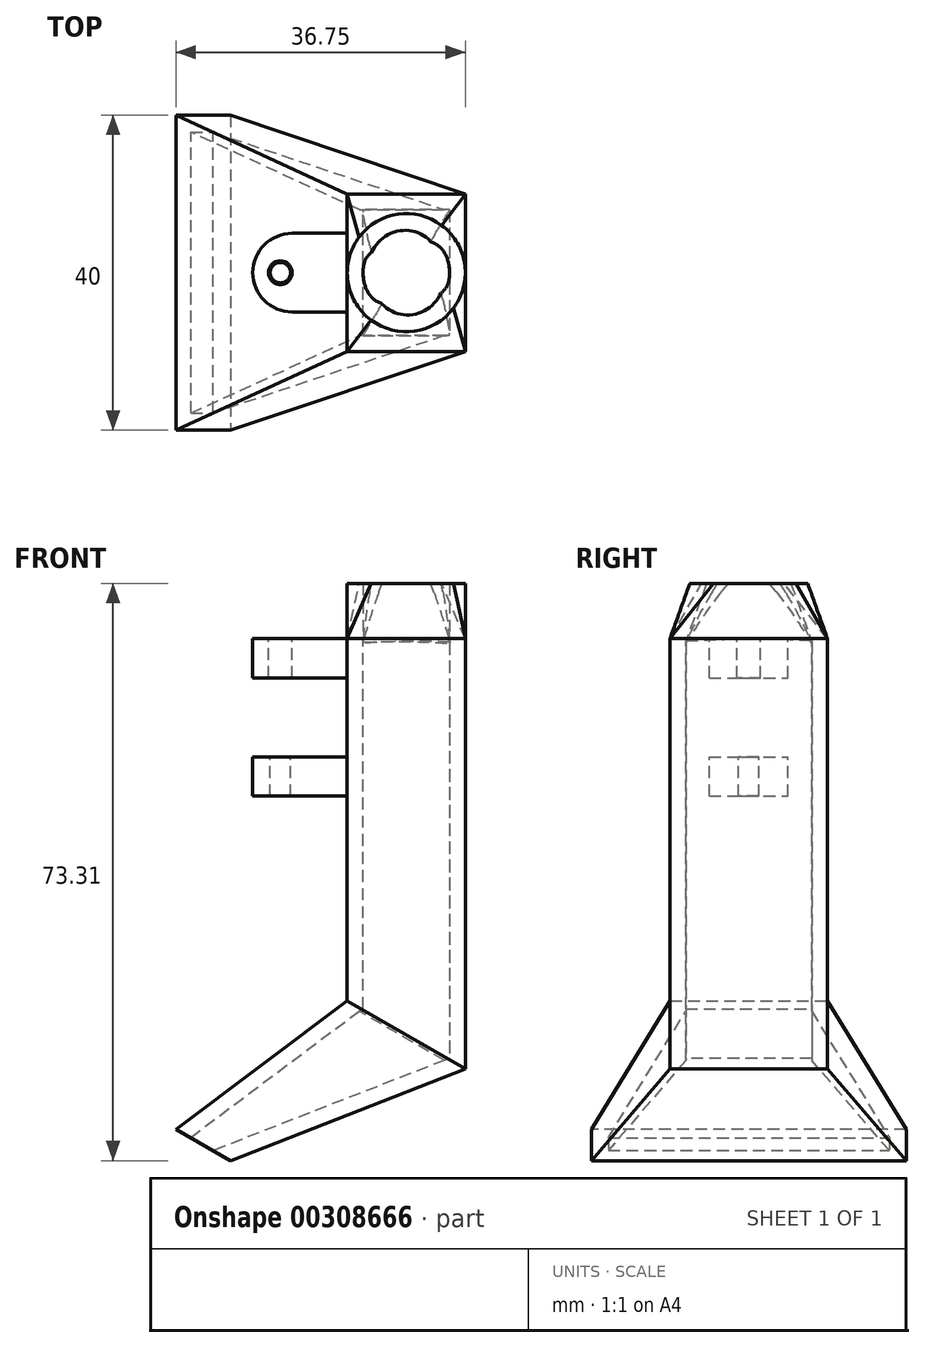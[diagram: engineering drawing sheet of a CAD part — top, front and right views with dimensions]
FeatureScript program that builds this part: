
annotation { "Feature Type Name" : "Feature", "Feature Type Description" : "" }
export const myFeature = defineFeature(function(context is Context, id is Id, definition is map)
    precondition{}
    {
        {
            var Q0;
            Q0=qCreatedBy(makeId("Front.planeOp"),FACE);
            var sketch = newSketch(context, id + "F0", { "sketchPlane" : qUnion([Q0])});
            skLineSegment(sketch, "E0.top", {"start": v(7.5, 23) * mm, "end": v(-7.5, 23) * mm});
            skLineSegment(sketch, "E0.right", {"start": v(-7.5, -23) * mm, "end": v(-7.5, 23) * mm});
            skPoint(sketch, "E0.middle", {"position": v(0, 0) * mm});
            skLineSegment(sketch, "E1", {"start": v(7.5, 23) * mm, "end": v(7.5, -31.66) * mm});
            skLineSegment(sketch, "E2", {"start": v(-7.5, -23) * mm, "end": v(7.5, -31.66) * mm});
            skLineSegment(sketch, "E3.bottom", {"start": v(-7.5, 23) * mm, "end": v(-19.5, 23) * mm});
            skLineSegment(sketch, "E3.top", {"start": v(-7.5, 18) * mm, "end": v(-19.5, 18) * mm});
            skLineSegment(sketch, "E3.left", {"start": v(-7.5, 23) * mm, "end": v(-7.5, 18) * mm});
            skLineSegment(sketch, "E3.right", {"start": v(-19.5, 23) * mm, "end": v(-19.5, 18) * mm});
            skLineSegment(sketch, "E4.bottom", {"start": v(-7.5, 8) * mm, "end": v(-19.5, 8) * mm});
            skLineSegment(sketch, "E4.top", {"start": v(-7.5, 3) * mm, "end": v(-19.5, 3) * mm});
            skLineSegment(sketch, "E4.left", {"start": v(-7.5, 8) * mm, "end": v(-7.5, 3) * mm});
            skLineSegment(sketch, "E4.right", {"start": v(-19.5, 8) * mm, "end": v(-19.5, 3) * mm});
            skLineSegment(sketch, "E5", {"start": v(-16, 23) * mm, "end": v(-16, 18) * mm});
            skLineSegment(sketch, "E6.0", {"start": v(-17.5, 23) * mm, "end": v(-17.5, 18) * mm});
            skLineSegment(sketch, "E7", {"start": v(-16, 8) * mm, "end": v(-16, 3) * mm});
            skLineSegment(sketch, "E8.0", {"start": v(-17.3, 8) * mm, "end": v(-17.3, 3) * mm});
            skSolve(sketch);
        }
        {
            var Q0;
            Q0=makeQuery(id+"F0.imprint","IMPRINT",FACE,{"disambiguationData":[TD([[makeQuery(id+"F0.imprint","IMPRINT",EDGE,{"derivedFrom":sQuery(id+"F0.wireOp",EDGE,"E0.top")}),1.0]])]});
            extrude(context, id + "F1", {"entities" : qUnion([Q0]), "depth" : 20 * mm});
        }
        {
            var Q0;
            Q0=makeQuery(id+"F1.opExtrude","SWEPT_FACE",FACE,{"disambiguationData":[OSD([sQuery(id+"F0.wireOp",EDGE,"E2")])]});
            cPlane(context, id + "F2", {"entities" : qUnion([Q0]), "cplaneType" : CPlaneType.OFFSET, "offset" : 25 * mm, "width" : 150 * mm, "height" : 150 * mm});
        }
        {
            var Q0;
            Q0=qCreatedBy(id+"F2.planeOp",FACE);
            var sketch = newSketch(context, id + "F3", { "sketchPlane" : qUnion([Q0])});
            skLineSegment(sketch, "E9.bottom", {"start": v(-5.67, -10) * mm, "end": v(2.33, -10) * mm});
            skLineSegment(sketch, "E9.top", {"start": v(-5.67, 30) * mm, "end": v(2.33, 30) * mm});
            skLineSegment(sketch, "E9.left", {"start": v(-5.67, -10) * mm, "end": v(-5.67, 30) * mm});
            skLineSegment(sketch, "E9.right", {"start": v(2.33, -10) * mm, "end": v(2.33, 30) * mm});
            skSolve(sketch);
        }
        {
            var Q1;
            Q1=makeQuery(id+"F1.opExtrude","SWEPT_FACE",FACE,{"disambiguationData":[OSD([sQuery(id+"F0.wireOp",EDGE,"E2")])]});
            var Q2;
            Q2=makeQuery(id+"F3.imprint","IMPRINT",FACE,{"disambiguationData":[TD([[makeQuery(id+"F3.imprint","IMPRINT",EDGE,{"derivedFrom":sQuery(id+"F3.wireOp",EDGE,"E9.bottom")}),1.0]])]});
            loft(context, id + "F4", {"operationType" : NewBodyOperationType.ADD, "sheetProfilesArray" : [{ "sheetProfileEntities" : qUnion([Q1]) }, { "sheetProfileEntities" : qUnion([Q2]) }]});
        }
        {
            var Q0;
            Q0=makeQuery(id+"F1.opExtrude","SWEPT_FACE",FACE,{"disambiguationData":[OSD([sQuery(id+"F0.wireOp",EDGE,"E0.top")])]});
            cPlane(context, id + "F5", {"entities" : qUnion([Q0]), "cplaneType" : CPlaneType.OFFSET, "offset" : 7 * mm, "width" : 150 * mm, "height" : 150 * mm});
        }
        {
            var Q0;
            Q0=qCreatedBy(id+"F5.planeOp",FACE);
            var sketch = newSketch(context, id + "F6", { "sketchPlane" : qUnion([Q0])});
            skCircle(sketch, "E10", {"center": v(0, -10) * mm, "radius": 7.5 * mm});
            skSolve(sketch);
        }
        {
            var Q1;
            Q1=makeQuery(id+"F1.opExtrude","SWEPT_FACE",FACE,{"disambiguationData":[OSD([sQuery(id+"F0.wireOp",EDGE,"E0.top")])]});
            var Q2;
            Q2=makeQuery(id+"F6.imprint","IMPRINT",FACE,{"disambiguationData":[TD([[makeQuery(id+"F6.imprint","IMPRINT",EDGE,{"derivedFrom":sQuery(id+"F6.wireOp",EDGE,"E10")}),1.0]])]});
            loft(context, id + "F7", {"operationType" : NewBodyOperationType.ADD, "sheetProfilesArray" : [{ "sheetProfileEntities" : qUnion([Q1]) }, { "sheetProfileEntities" : qUnion([Q2]) }]});
        }
        {
            var Q0;
            Q0=makeQuery(id+"F4.opLoft","CAP_FACE",FACE,{"disambiguationData":[OSD([makeQuery(id+"F3.imprint","IMPRINT",FACE,{"disambiguationData":[TD([[makeQuery(id+"F3.imprint","IMPRINT",EDGE,{"derivedFrom":sQuery(id+"F3.wireOp",EDGE,"E9.bottom")}),1.0]])]})])],"isStart":true});
            var Q1;
            Q1=makeQuery(id+"F7.opLoft","CAP_FACE",FACE,{"disambiguationData":[OSD([makeQuery(id+"F6.imprint","IMPRINT",FACE,{"disambiguationData":[TD([[makeQuery(id+"F6.imprint","IMPRINT",EDGE,{"derivedFrom":sQuery(id+"F6.wireOp",EDGE,"E10")}),1.0]])]})])],"isStart":true});
            shell(context, id + "F8", {"entities" : qUnion([Q0, Q1]), "thickness" : 2 * mm});
        }
        {
            var Q0;
            Q0=makeQuery(id+"F0.imprint","IMPRINT",FACE,{"disambiguationData":[TD([[makeQuery(id+"F0.imprint","IMPRINT",EDGE,{"derivedFrom":sQuery(id+"F0.wireOp",EDGE,"E3.bottom")}),1.0]])]});
            var Q1;
            Q1=makeQuery(id+"F0.imprint","IMPRINT",FACE,{"disambiguationData":[TD([[makeQuery(id+"F0.imprint","IMPRINT",EDGE,{"derivedFrom":sQuery(id+"F0.wireOp",EDGE,"E4.bottom")}),1.0]])]});
            var Q2;
            {var subQ0=sQuery(id+"F0.wireOp",EDGE,"E7");Q2=makeQuery(id+"F0.imprint","IMPRINT",FACE,{"disambiguationData":[TD([[makeQuery(id+"F0.imprint","IMPRINT",EDGE,{"derivedFrom":subQ0}),-1.0]])]});}
            var Q3;
            {var subQ0=sQuery(id+"F0.wireOp",EDGE,"E4.left");Q3=makeQuery(id+"F0.imprint","IMPRINT",FACE,{"disambiguationData":[TD([[makeQuery(id+"F0.imprint","IMPRINT",EDGE,{"derivedFrom":subQ0}),-1.0]])]});}
            extrude(context, id + "F9", {"entities" : qUnion([Q0, Q1, Q2, Q3]), "operationType" : NewBodyOperationType.ADD, "depth" : 15 * mm, "hasSecondDirection" : true, "secondDirectionOppositeDirection" : false, "secondDirectionDepth" : 5 * mm});
        }
        {
            var Q0;
            Q0=makeQuery(id+"F9.opExtrude","CAP_EDGE",EDGE,{"disambiguationData":[OSD([sQuery(id+"F0.wireOp",EDGE,"E3.left")])],"isStart":false});
            var Q1;
            Q1=makeQuery(id+"F9.opExtrude","CAP_EDGE",EDGE,{"disambiguationData":[OSD([sQuery(id+"F0.wireOp",EDGE,"E4.left")])],"isStart":false});
            var Q2;
            Q2=makeQuery(id+"F9.opExtrude","CAP_EDGE",EDGE,{"disambiguationData":[OSD([sQuery(id+"F0.wireOp",EDGE,"E3.left")])],"isStart":true});
            var Q3;
            Q3=makeQuery(id+"F9.opExtrude","CAP_EDGE",EDGE,{"disambiguationData":[OSD([sQuery(id+"F0.wireOp",EDGE,"E4.left")])],"isStart":true});
            var Q4;
            Q4=makeQuery(id+"F9.opExtrude","CAP_EDGE",EDGE,{"disambiguationData":[OSD([sQuery(id+"F0.wireOp",EDGE,"E4.right")])],"isStart":true});
            var Q5;
            Q5=makeQuery(id+"F9.opExtrude","CAP_EDGE",EDGE,{"disambiguationData":[OSD([sQuery(id+"F0.wireOp",EDGE,"E3.right")])],"isStart":true});
            var Q6;
            Q6=makeQuery(id+"F9.opExtrude","CAP_EDGE",EDGE,{"disambiguationData":[OSD([sQuery(id+"F0.wireOp",EDGE,"E3.right")])],"isStart":false});
            var Q7;
            Q7=makeQuery(id+"F9.opExtrude","CAP_EDGE",EDGE,{"disambiguationData":[OSD([sQuery(id+"F0.wireOp",EDGE,"E4.right")])],"isStart":false});
            fillet(context, id + "F10", {"entities" : qUnion([Q0, Q1, Q2, Q3, Q4, Q5, Q6, Q7]), "radius" : 5 * mm, "tangentPropagation" : true, "allowEdgeOverflow" : false});
        }
        {
            var Q0;
            {var subQ0=sQuery(id+"F0.wireOp",EDGE,"E5");Q0=makeQuery(id+"F0.imprint","IMPRINT",FACE,{"disambiguationData":[TD([[makeQuery(id+"F0.imprint","IMPRINT",EDGE,{"derivedFrom":subQ0}),-1.0]])]});}
            var Q1;
            Q1=sQuery(id+"F0.wireOp",EDGE,"E5");
            revolve(context, id + "F11", {"entities" : qUnion([Q0]), "axis" : qUnion([Q1]), "revolveType" : RevolveType.FULL});
        }
        {
            var Q0;
            {var subQ0=sQuery(id+"F0.wireOp",EDGE,"E7");Q0=makeQuery(id+"F0.imprint","IMPRINT",FACE,{"disambiguationData":[TD([[makeQuery(id+"F0.imprint","IMPRINT",EDGE,{"derivedFrom":subQ0}),-1.0]])]});}
            var Q1;
            Q1=sQuery(id+"F0.wireOp",EDGE,"E7");
            revolve(context, id + "F12", {"entities" : qUnion([Q0]), "axis" : qUnion([Q1]), "revolveType" : RevolveType.FULL});
        }
        {
            var Q0;
            Q0=makeQuery(id+"F11.opRevolve","SWEPT_BODY",BODY,{"disambiguationData":[OSD([sQuery(id+"F0.wireOp",EDGE,"E3.bottom"),sQuery(id+"F0.wireOp",EDGE,"E3.top"),sQuery(id+"F0.wireOp",EDGE,"E5"),sQuery(id+"F0.wireOp",EDGE,"E6.0")])]});
            var Q1;
            Q1=makeQuery(id+"F12.opRevolve","SWEPT_BODY",BODY,{"disambiguationData":[OSD([sQuery(id+"F0.wireOp",EDGE,"E4.bottom"),sQuery(id+"F0.wireOp",EDGE,"E4.top"),sQuery(id+"F0.wireOp",EDGE,"E7"),sQuery(id+"F0.wireOp",EDGE,"E8.0")])]});
            transform(context, id + "F13", {"entities" : qUnion([Q0, Q1]), "transformType" : TransformType.TRANSLATION_3D, "dx" : 0 * mm, "dy" : -10 * mm, "dz" : 0 * mm, "makeCopy" : false});
        }
        {
            var Q0;
            Q0=makeQuery(id+"F11.opRevolve","SWEPT_BODY",BODY,{"disambiguationData":[OSD([sQuery(id+"F0.wireOp",EDGE,"E3.bottom"),sQuery(id+"F0.wireOp",EDGE,"E3.top"),sQuery(id+"F0.wireOp",EDGE,"E5"),sQuery(id+"F0.wireOp",EDGE,"E6.0")])]});
            var Q1;
            Q1=makeQuery(id+"F12.opRevolve","SWEPT_BODY",BODY,{"disambiguationData":[OSD([sQuery(id+"F0.wireOp",EDGE,"E4.bottom"),sQuery(id+"F0.wireOp",EDGE,"E4.top"),sQuery(id+"F0.wireOp",EDGE,"E7"),sQuery(id+"F0.wireOp",EDGE,"E8.0")])]});
            var Q2;
            Q2=makeQuery(id+"F1.opExtrude","SWEPT_BODY",BODY,{"disambiguationData":[OSD([sQuery(id+"F0.wireOp",EDGE,"E0.top"),sQuery(id+"F0.wireOp",EDGE,"E0.right"),sQuery(id+"F0.wireOp",EDGE,"E1"),sQuery(id+"F0.wireOp",EDGE,"E2"),sQuery(id+"F0.wireOp",EDGE,"E3.left"),sQuery(id+"F0.wireOp",EDGE,"E4.left")])]});
            booleanBodies(context, id + "F14", {"operationType" : BooleanOperationType.SUBTRACTION, "tools" : qUnion([Q0, Q1]), "targets" : qUnion([Q2])});
        }
    });
